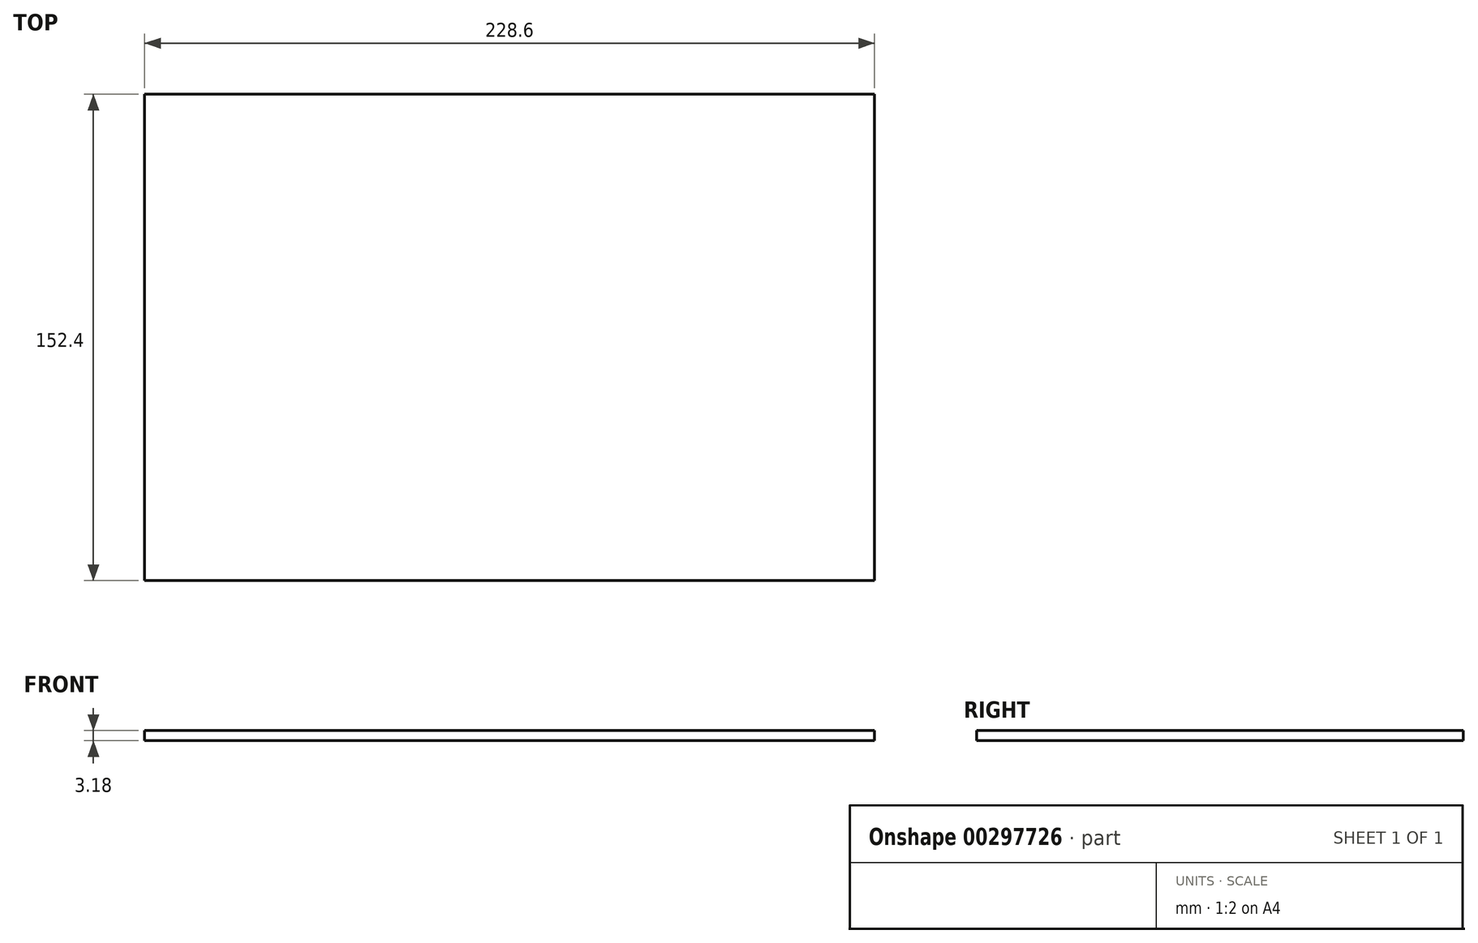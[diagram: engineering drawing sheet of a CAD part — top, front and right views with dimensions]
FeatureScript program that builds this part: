
annotation { "Feature Type Name" : "Feature", "Feature Type Description" : "" }
export const myFeature = defineFeature(function(context is Context, id is Id, definition is map)
    precondition{}
    {
        {
            var Q0;
            Q0=qCreatedBy(makeId("Top.planeOp"),FACE);
            var sketch = newSketch(context, id + "F0", { "sketchPlane" : qUnion([Q0])});
            skLineSegment(sketch, "E0.bottom", {"start": v(114.3, -76.2) * mm, "end": v(-114.3, -76.2) * mm});
            skLineSegment(sketch, "E0.top", {"start": v(114.3, 76.2) * mm, "end": v(-114.3, 76.2) * mm});
            skLineSegment(sketch, "E0.left", {"start": v(114.3, -76.2) * mm, "end": v(114.3, 76.2) * mm});
            skLineSegment(sketch, "E0.right", {"start": v(-114.3, -76.2) * mm, "end": v(-114.3, 76.2) * mm});
            skPoint(sketch, "E0.middle", {"position": v(0, 0) * mm});
            skSolve(sketch);
        }
        {
            var Q0;
            Q0 = qSketchRegion(id + "F0", true);
            extrude(context, id + "F1", {"entities" : qUnion([Q0]), "endBound" : BoundingType.SYMMETRIC, "depth" : 3.17 * mm});
        }
    });
